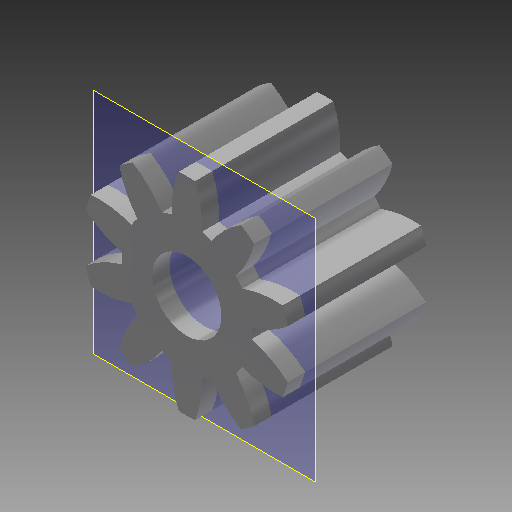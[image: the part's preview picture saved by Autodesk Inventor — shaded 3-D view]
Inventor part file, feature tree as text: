
AUTODESK INVENTOR PART (.ipt)
format: ipt  version: 2017 (Build 210142000, 142)  size: 212,992 bytes
history: native  units: mm (DEFAULTED — no unit token found)
features: plane x4, other x3, sketch x3, extrude x2
ambient origin geometry x8: Origin, YZ Plane, XZ Plane, XY Plane, X Axis, Y Axis, Z Axis, Center Point
bodies: Solid1 (feature_tree)
feature tree (12):
  extrude  "Extrusion1"  Depth=4.0mm TaperAngle=0.0deg
  plane  "Work Plane2"
  plane  "Work Plane8"
  plane  "Work Plane9"
  other  "Spur Gear"
  extrude  "Extrusion2"  Depth=10.0mm TaperAngle=0.0deg
  plane  "Work Plane12"
  sketch  "Sketch1"  dims[d0=6.0mm d1=4.0mm d2=0.0mm]
  sketch  "Sketch2"  dims[d3=5.0mm d4=10.0mm d5=0.0mm]
  other  "Srf1"
  sketch  "Sketch3"  dims[d16=11.5mm d17=0.0mm d34=3.141593mm d39=0.0mm d41=0.0mm d43=11.5mm d46=11.5mm d47=0.0mm d48=0.0mm d49=2.0mm d50=10.0mm d51=0.0mm d53=-3.5mm]
  other  "Pitch Diameter"
